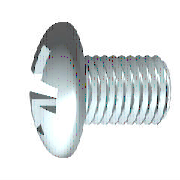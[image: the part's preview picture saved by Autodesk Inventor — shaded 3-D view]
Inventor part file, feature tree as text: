
AUTODESK INVENTOR PART (.ipt)
format: ipt  version: 2024.1 (Build 281209000, 209)  size: 271,872 bytes
history: native  units: mm (DEFAULTED — no unit token found)
features: extrude x1, other x1, plane x1
ambient origin geometry x7: Origin, YZ Plane, XZ Plane, X Axis, Y Axis, Z Axis, Center Point
bodies: Solid1 (feature_tree), Body (feature_tree)
feature tree (3):
  extrude  "Slot"  Depth=2.5mm
  other  "Cut"
  plane  "Work Plane3"
